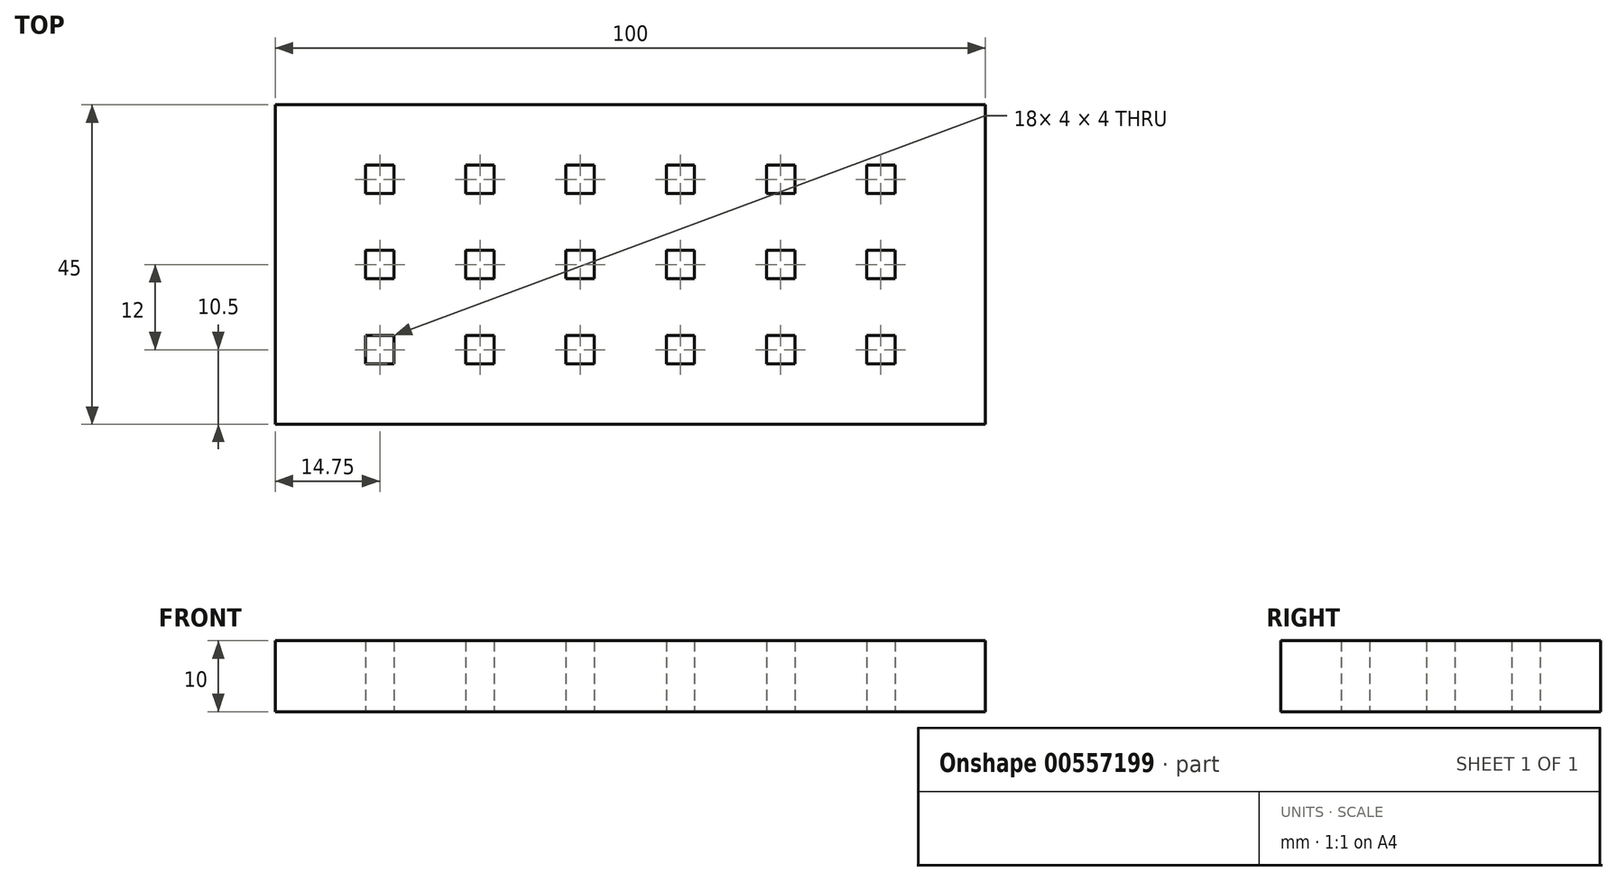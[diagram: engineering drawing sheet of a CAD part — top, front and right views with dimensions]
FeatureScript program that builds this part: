
annotation { "Feature Type Name" : "Feature", "Feature Type Description" : "" }
export const myFeature = defineFeature(function(context is Context, id is Id, definition is map)
    precondition{}
    {
        {
            var Q0;
            Q0=qCreatedBy(makeId("Top.planeOp"),FACE);
            var sketch = newSketch(context, id + "F0", { "sketchPlane" : qUnion([Q0])});
            skLineSegment(sketch, "E0.bottom", {"start": v(0, 0) * mm, "end": v(100, 0) * mm});
            skLineSegment(sketch, "E0.top", {"start": v(0, 45) * mm, "end": v(100, 45) * mm});
            skLineSegment(sketch, "E0.left", {"start": v(0, 0) * mm, "end": v(0, 45) * mm});
            skLineSegment(sketch, "E0.right", {"start": v(100, 0) * mm, "end": v(100, 45) * mm});
            skLineSegment(sketch, "E1.bottom", {"start": v(12.75, 8.5) * mm, "end": v(16.75, 8.5) * mm});
            skLineSegment(sketch, "E1.top", {"start": v(12.75, 12.5) * mm, "end": v(16.75, 12.5) * mm});
            skLineSegment(sketch, "E1.left", {"start": v(12.75, 8.5) * mm, "end": v(12.75, 12.5) * mm});
            skLineSegment(sketch, "E1.right", {"start": v(16.75, 8.5) * mm, "end": v(16.75, 12.5) * mm});
            skLineSegment(sketch, "E2.0.1.0", {"start": v(12.75, 24.5) * mm, "end": v(16.75, 24.5) * mm});
            skLineSegment(sketch, "E2.0.1.1", {"start": v(12.75, 20.5) * mm, "end": v(12.75, 24.5) * mm});
            skLineSegment(sketch, "E2.0.1.2", {"start": v(12.75, 20.5) * mm, "end": v(16.75, 20.5) * mm});
            skLineSegment(sketch, "E2.0.1.3", {"start": v(16.75, 20.5) * mm, "end": v(16.75, 24.5) * mm});
            skLineSegment(sketch, "E2.0.2.0", {"start": v(12.75, 36.5) * mm, "end": v(16.75, 36.5) * mm});
            skLineSegment(sketch, "E2.0.2.1", {"start": v(12.75, 32.5) * mm, "end": v(12.75, 36.5) * mm});
            skLineSegment(sketch, "E2.0.2.2", {"start": v(12.75, 32.5) * mm, "end": v(16.75, 32.5) * mm});
            skLineSegment(sketch, "E2.0.2.3", {"start": v(16.75, 32.5) * mm, "end": v(16.75, 36.5) * mm});
            skLineSegment(sketch, "E2.1.0.0", {"start": v(26.85, 12.5) * mm, "end": v(30.85, 12.5) * mm});
            skLineSegment(sketch, "E2.1.0.1", {"start": v(26.85, 8.5) * mm, "end": v(26.85, 12.5) * mm});
            skLineSegment(sketch, "E2.1.0.2", {"start": v(26.85, 8.5) * mm, "end": v(30.85, 8.5) * mm});
            skLineSegment(sketch, "E2.1.0.3", {"start": v(30.85, 8.5) * mm, "end": v(30.85, 12.5) * mm});
            skLineSegment(sketch, "E2.1.1.0", {"start": v(26.85, 24.5) * mm, "end": v(30.85, 24.5) * mm});
            skLineSegment(sketch, "E2.1.1.1", {"start": v(26.85, 20.5) * mm, "end": v(26.85, 24.5) * mm});
            skLineSegment(sketch, "E2.1.1.2", {"start": v(26.85, 20.5) * mm, "end": v(30.85, 20.5) * mm});
            skLineSegment(sketch, "E2.1.1.3", {"start": v(30.85, 20.5) * mm, "end": v(30.85, 24.5) * mm});
            skLineSegment(sketch, "E2.1.2.0", {"start": v(26.85, 36.5) * mm, "end": v(30.85, 36.5) * mm});
            skLineSegment(sketch, "E2.1.2.1", {"start": v(26.85, 32.5) * mm, "end": v(26.85, 36.5) * mm});
            skLineSegment(sketch, "E2.1.2.2", {"start": v(26.85, 32.5) * mm, "end": v(30.85, 32.5) * mm});
            skLineSegment(sketch, "E2.1.2.3", {"start": v(30.85, 32.5) * mm, "end": v(30.85, 36.5) * mm});
            skLineSegment(sketch, "E2.2.0.0", {"start": v(40.95, 12.5) * mm, "end": v(44.95, 12.5) * mm});
            skLineSegment(sketch, "E2.2.0.1", {"start": v(40.95, 8.5) * mm, "end": v(40.95, 12.5) * mm});
            skLineSegment(sketch, "E2.2.0.2", {"start": v(40.95, 8.5) * mm, "end": v(44.95, 8.5) * mm});
            skLineSegment(sketch, "E2.2.0.3", {"start": v(44.95, 8.5) * mm, "end": v(44.95, 12.5) * mm});
            skLineSegment(sketch, "E2.2.1.0", {"start": v(40.95, 24.5) * mm, "end": v(44.95, 24.5) * mm});
            skLineSegment(sketch, "E2.2.1.1", {"start": v(40.95, 20.5) * mm, "end": v(40.95, 24.5) * mm});
            skLineSegment(sketch, "E2.2.1.2", {"start": v(40.95, 20.5) * mm, "end": v(44.95, 20.5) * mm});
            skLineSegment(sketch, "E2.2.1.3", {"start": v(44.95, 20.5) * mm, "end": v(44.95, 24.5) * mm});
            skLineSegment(sketch, "E2.2.2.0", {"start": v(40.95, 36.5) * mm, "end": v(44.95, 36.5) * mm});
            skLineSegment(sketch, "E2.2.2.1", {"start": v(40.95, 32.5) * mm, "end": v(40.95, 36.5) * mm});
            skLineSegment(sketch, "E2.2.2.2", {"start": v(40.95, 32.5) * mm, "end": v(44.95, 32.5) * mm});
            skLineSegment(sketch, "E2.2.2.3", {"start": v(44.95, 32.5) * mm, "end": v(44.95, 36.5) * mm});
            skLineSegment(sketch, "E2.3.0.0", {"start": v(55.05, 12.5) * mm, "end": v(59.05, 12.5) * mm});
            skLineSegment(sketch, "E2.3.0.1", {"start": v(55.05, 8.5) * mm, "end": v(55.05, 12.5) * mm});
            skLineSegment(sketch, "E2.3.0.2", {"start": v(55.05, 8.5) * mm, "end": v(59.05, 8.5) * mm});
            skLineSegment(sketch, "E2.3.0.3", {"start": v(59.05, 8.5) * mm, "end": v(59.05, 12.5) * mm});
            skLineSegment(sketch, "E2.3.1.0", {"start": v(55.05, 24.5) * mm, "end": v(59.05, 24.5) * mm});
            skLineSegment(sketch, "E2.3.1.1", {"start": v(55.05, 20.5) * mm, "end": v(55.05, 24.5) * mm});
            skLineSegment(sketch, "E2.3.1.2", {"start": v(55.05, 20.5) * mm, "end": v(59.05, 20.5) * mm});
            skLineSegment(sketch, "E2.3.1.3", {"start": v(59.05, 20.5) * mm, "end": v(59.05, 24.5) * mm});
            skLineSegment(sketch, "E2.3.2.0", {"start": v(55.05, 36.5) * mm, "end": v(59.05, 36.5) * mm});
            skLineSegment(sketch, "E2.3.2.1", {"start": v(55.05, 32.5) * mm, "end": v(55.05, 36.5) * mm});
            skLineSegment(sketch, "E2.3.2.2", {"start": v(55.05, 32.5) * mm, "end": v(59.05, 32.5) * mm});
            skLineSegment(sketch, "E2.3.2.3", {"start": v(59.05, 32.5) * mm, "end": v(59.05, 36.5) * mm});
            skLineSegment(sketch, "E2.4.0.0", {"start": v(69.15, 12.5) * mm, "end": v(73.15, 12.5) * mm});
            skLineSegment(sketch, "E2.4.0.1", {"start": v(69.15, 8.5) * mm, "end": v(69.15, 12.5) * mm});
            skLineSegment(sketch, "E2.4.0.2", {"start": v(69.15, 8.5) * mm, "end": v(73.15, 8.5) * mm});
            skLineSegment(sketch, "E2.4.0.3", {"start": v(73.15, 8.5) * mm, "end": v(73.15, 12.5) * mm});
            skLineSegment(sketch, "E2.4.1.0", {"start": v(69.15, 24.5) * mm, "end": v(73.15, 24.5) * mm});
            skLineSegment(sketch, "E2.4.1.1", {"start": v(69.15, 20.5) * mm, "end": v(69.15, 24.5) * mm});
            skLineSegment(sketch, "E2.4.1.2", {"start": v(69.15, 20.5) * mm, "end": v(73.15, 20.5) * mm});
            skLineSegment(sketch, "E2.4.1.3", {"start": v(73.15, 20.5) * mm, "end": v(73.15, 24.5) * mm});
            skLineSegment(sketch, "E2.4.2.0", {"start": v(69.15, 36.5) * mm, "end": v(73.15, 36.5) * mm});
            skLineSegment(sketch, "E2.4.2.1", {"start": v(69.15, 32.5) * mm, "end": v(69.15, 36.5) * mm});
            skLineSegment(sketch, "E2.4.2.2", {"start": v(69.15, 32.5) * mm, "end": v(73.15, 32.5) * mm});
            skLineSegment(sketch, "E2.4.2.3", {"start": v(73.15, 32.5) * mm, "end": v(73.15, 36.5) * mm});
            skLineSegment(sketch, "E2.5.0.0", {"start": v(83.25, 12.5) * mm, "end": v(87.25, 12.5) * mm});
            skLineSegment(sketch, "E2.5.0.1", {"start": v(83.25, 8.5) * mm, "end": v(83.25, 12.5) * mm});
            skLineSegment(sketch, "E2.5.0.2", {"start": v(83.25, 8.5) * mm, "end": v(87.25, 8.5) * mm});
            skLineSegment(sketch, "E2.5.0.3", {"start": v(87.25, 8.5) * mm, "end": v(87.25, 12.5) * mm});
            skLineSegment(sketch, "E2.5.1.0", {"start": v(83.25, 24.5) * mm, "end": v(87.25, 24.5) * mm});
            skLineSegment(sketch, "E2.5.1.1", {"start": v(83.25, 20.5) * mm, "end": v(83.25, 24.5) * mm});
            skLineSegment(sketch, "E2.5.1.2", {"start": v(83.25, 20.5) * mm, "end": v(87.25, 20.5) * mm});
            skLineSegment(sketch, "E2.5.1.3", {"start": v(87.25, 20.5) * mm, "end": v(87.25, 24.5) * mm});
            skLineSegment(sketch, "E2.5.2.0", {"start": v(83.25, 36.5) * mm, "end": v(87.25, 36.5) * mm});
            skLineSegment(sketch, "E2.5.2.1", {"start": v(83.25, 32.5) * mm, "end": v(83.25, 36.5) * mm});
            skLineSegment(sketch, "E2.5.2.2", {"start": v(83.25, 32.5) * mm, "end": v(87.25, 32.5) * mm});
            skLineSegment(sketch, "E2.5.2.3", {"start": v(87.25, 32.5) * mm, "end": v(87.25, 36.5) * mm});
            skLineSegment(sketch, "E2.direction1", {"start": v(12.75, 8.5) * mm, "end": v(26.85, 8.5) * mm, "construction": true});
            skLineSegment(sketch, "E2.direction2", {"start": v(12.75, 8.5) * mm, "end": v(12.75, 20.5) * mm, "construction": true});
            skSolve(sketch);
        }
        {
            var Q0;
            Q0=makeQuery(id+"F0.imprint","IMPRINT",FACE,{"disambiguationData":[TD([[makeQuery(id+"F0.imprint","IMPRINT",EDGE,{"derivedFrom":sQuery(id+"F0.wireOp",EDGE,"E0.bottom")}),1.0]])]});
            extrude(context, id + "F1", {"entities" : qUnion([Q0]), "depth" : 10 * mm, "offsetDistance" : 25 * mm});
        }
    });
